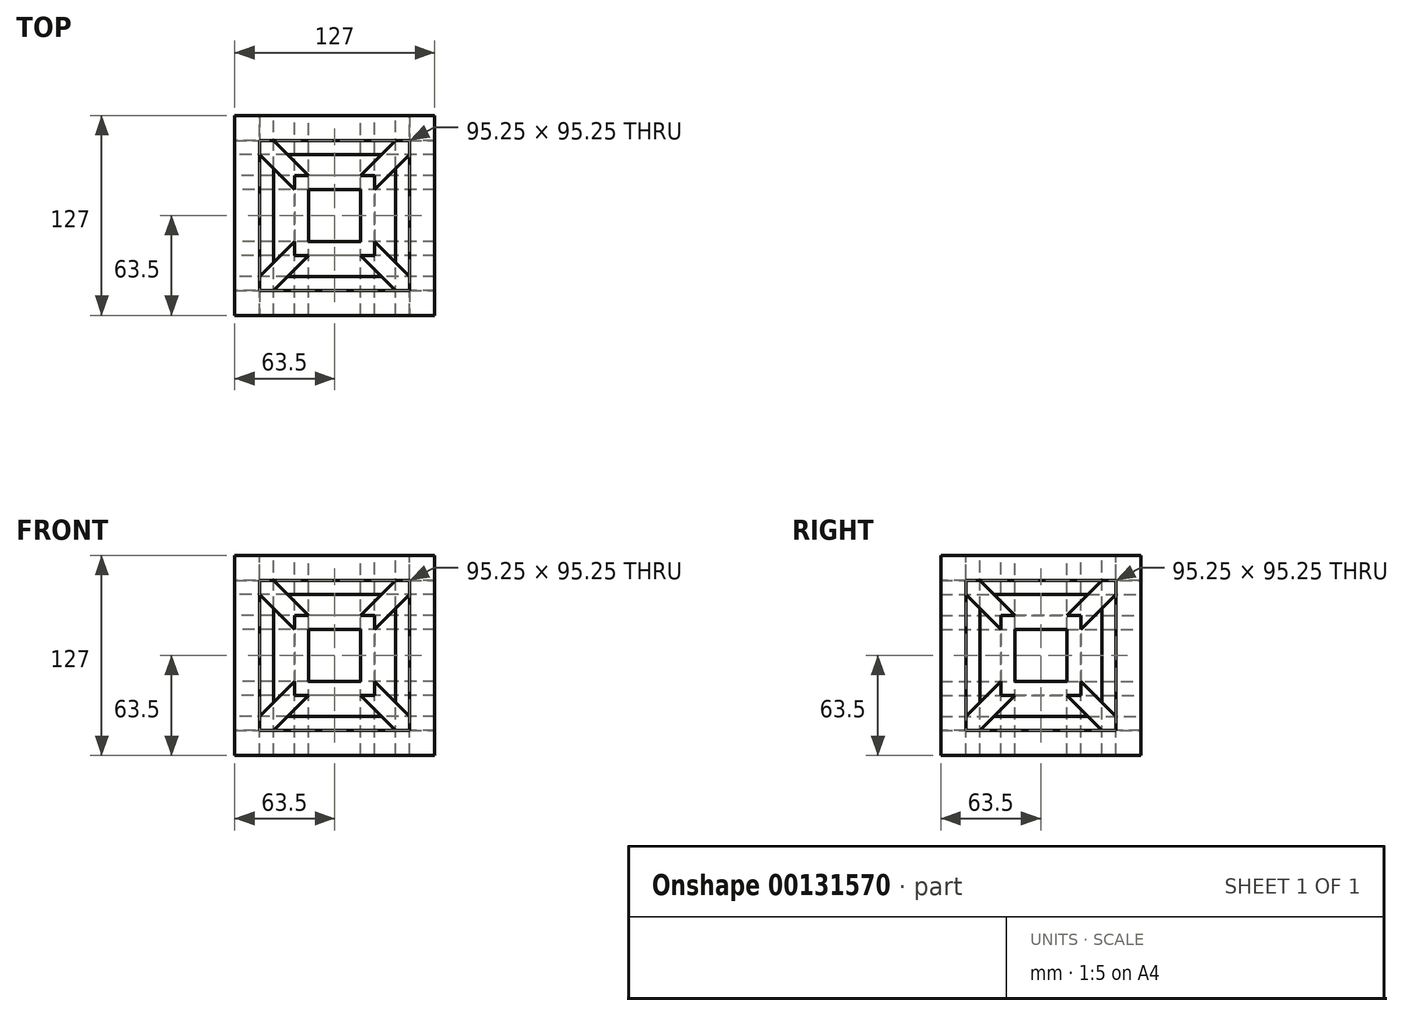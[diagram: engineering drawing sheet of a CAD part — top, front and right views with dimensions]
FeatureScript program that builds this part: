
annotation { "Feature Type Name" : "Feature", "Feature Type Description" : "" }
export const myFeature = defineFeature(function(context is Context, id is Id, definition is map)
    precondition{}
    {
        {
            var Q0;
            Q0=qCreatedBy(makeId("Front.planeOp"),FACE);
            var sketch = newSketch(context, id + "F0", { "sketchPlane" : qUnion([Q0])});
            skLineSegment(sketch, "E0.bottom", {"start": v(63.5, 63.5) * mm, "end": v(-63.5, 63.5) * mm});
            skLineSegment(sketch, "E0.top", {"start": v(63.5, -63.5) * mm, "end": v(-63.5, -63.5) * mm});
            skLineSegment(sketch, "E0.left", {"start": v(63.5, 63.5) * mm, "end": v(63.5, -63.5) * mm});
            skLineSegment(sketch, "E0.right", {"start": v(-63.5, 63.5) * mm, "end": v(-63.5, -63.5) * mm});
            skPoint(sketch, "E0.middle", {"position": v(0, 0) * mm});
            skSolve(sketch);
        }
        {
            var Q0;
            Q0 = qSketchRegion(id + "F0", true);
            extrude(context, id + "F1", {"entities" : qUnion([Q0]), "endBound" : BoundingType.SYMMETRIC, "depth" : 127 * mm});
        }
        {
            var Q0;
            Q0=makeQuery(id+"F1.opExtrude","CAP_FACE",FACE,{"disambiguationData":[OSD([sQuery(id+"F0.wireOp",EDGE,"E0.bottom"),sQuery(id+"F0.wireOp",EDGE,"E0.top"),sQuery(id+"F0.wireOp",EDGE,"E0.left"),sQuery(id+"F0.wireOp",EDGE,"E0.right")])],"isStart":false});
            var sketch = newSketch(context, id + "F2", { "sketchPlane" : qUnion([Q0])});
            skLineSegment(sketch, "E1.bottom", {"start": v(47.63, 47.63) * mm, "end": v(-47.63, 47.63) * mm});
            skLineSegment(sketch, "E1.top", {"start": v(47.63, -47.62) * mm, "end": v(-47.63, -47.62) * mm});
            skLineSegment(sketch, "E1.left", {"start": v(47.63, 47.63) * mm, "end": v(47.63, -47.62) * mm});
            skLineSegment(sketch, "E1.right", {"start": v(-47.63, 47.63) * mm, "end": v(-47.63, -47.62) * mm});
            skPoint(sketch, "E1.middle", {"position": v(0, 0) * mm});
            skSolve(sketch);
        }
        {
            var Q0;
            Q0=makeQuery(id+"F1.opExtrude","SWEPT_FACE",FACE,{"disambiguationData":[OSD([sQuery(id+"F0.wireOp",EDGE,"E0.left")])]});
            var sketch = newSketch(context, id + "F3", { "sketchPlane" : qUnion([Q0])});
            skLineSegment(sketch, "E2.bottom", {"start": v(47.63, 47.63) * mm, "end": v(-47.63, 47.62) * mm});
            skLineSegment(sketch, "E2.top", {"start": v(47.63, -47.62) * mm, "end": v(-47.63, -47.63) * mm});
            skLineSegment(sketch, "E2.left", {"start": v(47.63, 47.62) * mm, "end": v(47.63, -47.63) * mm});
            skLineSegment(sketch, "E2.right", {"start": v(-47.63, 47.62) * mm, "end": v(-47.63, -47.63) * mm});
            skPoint(sketch, "E2.middle", {"position": v(0, 0) * mm});
            skSolve(sketch);
        }
        {
            var Q0;
            Q0=makeQuery(id+"F3.imprint","IMPRINT",FACE,{"disambiguationData":[TD([[makeQuery(id+"F3.imprint","IMPRINT",EDGE,{"derivedFrom":sQuery(id+"F3.wireOp",EDGE,"E2.bottom")}),1.0]])]});
            extrude(context, id + "F4", {"entities" : qUnion([Q0]), "operationType" : NewBodyOperationType.REMOVE, "oppositeDirection" : true, "depth" : 127 * mm});
        }
        {
            var Q0;
            Q0 = qSketchRegion(id + "F2", true);
            extrude(context, id + "F5", {"entities" : qUnion([Q0]), "operationType" : NewBodyOperationType.REMOVE, "oppositeDirection" : true, "depth" : 127 * mm});
        }
        {
            var Q0;
            Q0=makeQuery(id+"F1.opExtrude","SWEPT_FACE",FACE,{"disambiguationData":[OSD([sQuery(id+"F0.wireOp",EDGE,"E0.bottom")])]});
            var sketch = newSketch(context, id + "F6", { "sketchPlane" : qUnion([Q0])});
            skLineSegment(sketch, "E3.bottom", {"start": v(47.63, 47.63) * mm, "end": v(-47.63, 47.63) * mm});
            skLineSegment(sketch, "E3.top", {"start": v(47.63, -47.62) * mm, "end": v(-47.63, -47.62) * mm});
            skLineSegment(sketch, "E3.left", {"start": v(47.63, 47.63) * mm, "end": v(47.63, -47.62) * mm});
            skLineSegment(sketch, "E3.right", {"start": v(-47.63, 47.63) * mm, "end": v(-47.63, -47.62) * mm});
            skPoint(sketch, "E3.middle", {"position": v(0, 0) * mm});
            skSolve(sketch);
        }
        {
            var Q0;
            Q0 = qSketchRegion(id + "F6", true);
            extrude(context, id + "F7", {"entities" : qUnion([Q0]), "operationType" : NewBodyOperationType.REMOVE, "oppositeDirection" : true, "depth" : 127 * mm});
        }
        {
            var Q0;
            Q0=qCreatedBy(makeId("Top.planeOp"),FACE);
            var sketch = newSketch(context, id + "F8", { "sketchPlane" : qUnion([Q0])});
            skLineSegment(sketch, "E4.bottom", {"start": v(25.4, 25.4) * mm, "end": v(-25.4, 25.4) * mm});
            skLineSegment(sketch, "E4.top", {"start": v(25.4, -25.4) * mm, "end": v(-25.4, -25.4) * mm});
            skLineSegment(sketch, "E4.left", {"start": v(25.4, 25.4) * mm, "end": v(25.4, -25.4) * mm});
            skLineSegment(sketch, "E4.right", {"start": v(-25.4, 25.4) * mm, "end": v(-25.4, -25.4) * mm});
            skPoint(sketch, "E4.middle", {"position": v(0, 0) * mm});
            skSolve(sketch);
        }
        {
            var Q0;
            Q0 = qSketchRegion(id + "F8", true);
            extrude(context, id + "F9", {"entities" : qUnion([Q0]), "endBound" : BoundingType.SYMMETRIC, "depth" : 50.8 * mm});
        }
        {
            var Q0;
            Q0=qCreatedBy(makeId("Right.planeOp"),FACE);
            var sketch = newSketch(context, id + "F10", { "sketchPlane" : qUnion([Q0])});
            skLineSegment(sketch, "E5.bottom", {"start": v(25.4, 25.4) * mm, "end": v(-25.4, 25.4) * mm});
            skLineSegment(sketch, "E5.top", {"start": v(25.4, -25.4) * mm, "end": v(-25.4, -25.4) * mm});
            skLineSegment(sketch, "E5.left", {"start": v(25.4, 25.4) * mm, "end": v(25.4, -25.4) * mm});
            skLineSegment(sketch, "E5.right", {"start": v(-25.4, 25.4) * mm, "end": v(-25.4, -25.4) * mm});
            skPoint(sketch, "E5.middle", {"position": v(0, 0) * mm});
            skLineSegment(sketch, "E6.bottom", {"start": v(47.62, 47.63) * mm, "end": v(-47.63, 47.62) * mm});
            skLineSegment(sketch, "E6.top", {"start": v(47.63, -47.62) * mm, "end": v(-47.63, -47.63) * mm});
            skLineSegment(sketch, "E6.left", {"start": v(47.63, 47.63) * mm, "end": v(47.63, -47.62) * mm});
            skLineSegment(sketch, "E6.right", {"start": v(-47.63, 47.62) * mm, "end": v(-47.63, -47.63) * mm});
            skLineSegment(sketch, "E7", {"start": v(-16.5, 25.4) * mm, "end": v(-38.74, 47.62) * mm});
            skLineSegment(sketch, "E8", {"start": v(-25.4, 16.51) * mm, "end": v(-47.63, 38.73) * mm});
            skLineSegment(sketch, "E9", {"start": v(16.5, 25.4) * mm, "end": v(38.74, 47.63) * mm});
            skLineSegment(sketch, "E10", {"start": v(25.4, 16.51) * mm, "end": v(47.63, 38.73) * mm});
            skLineSegment(sketch, "E11", {"start": v(-25.4, -16.5) * mm, "end": v(-47.63, -38.74) * mm});
            skLineSegment(sketch, "E12", {"start": v(-16.5, -25.4) * mm, "end": v(-38.74, -47.63) * mm});
            skLineSegment(sketch, "E13", {"start": v(16.5, -25.4) * mm, "end": v(38.74, -47.62) * mm});
            skLineSegment(sketch, "E14", {"start": v(25.4, -16.5) * mm, "end": v(47.63, -38.74) * mm});
            skSolve(sketch);
        }
        {
            var Q0;
            {var subQ7=sQuery(id+"F10.wireOp",EDGE,"E7");Q0=makeQuery(id+"F10.imprint","IMPRINT",FACE,{"disambiguationData":[TD([[makeQuery(id+"F10.imprint","IMPRINT",EDGE,{"derivedFrom":subQ7}),1.0]])]});}
            var Q1;
            {var subQ4=sQuery(id+"F10.wireOp",EDGE,"E9");Q1=makeQuery(id+"F10.imprint","IMPRINT",FACE,{"disambiguationData":[TD([[makeQuery(id+"F10.imprint","IMPRINT",EDGE,{"derivedFrom":subQ4}),-1.0]])]});}
            var Q2;
            {var subQ7=sQuery(id+"F10.wireOp",EDGE,"E13");Q2=makeQuery(id+"F10.imprint","IMPRINT",FACE,{"disambiguationData":[TD([[makeQuery(id+"F10.imprint","IMPRINT",EDGE,{"derivedFrom":subQ7}),1.0]])]});}
            var Q3;
            {var subQ3=sQuery(id+"F10.wireOp",EDGE,"E11");Q3=makeQuery(id+"F10.imprint","IMPRINT",FACE,{"disambiguationData":[TD([[makeQuery(id+"F10.imprint","IMPRINT",EDGE,{"derivedFrom":subQ3}),1.0]])]});}
            extrude(context, id + "F11", {"entities" : qUnion([Q0, Q1, Q2, Q3]), "endBound" : BoundingType.SYMMETRIC, "depth" : 127 * mm});
        }
        {
            var Q0;
            Q0=qCreatedBy(makeId("Top.planeOp"),FACE);
            var sketch = newSketch(context, id + "F12", { "sketchPlane" : qUnion([Q0])});
            skLineSegment(sketch, "E15.bottom", {"start": v(25.4, 25.4) * mm, "end": v(-25.4, 25.4) * mm});
            skLineSegment(sketch, "E15.top", {"start": v(25.4, -25.4) * mm, "end": v(-25.4, -25.4) * mm});
            skLineSegment(sketch, "E15.left", {"start": v(25.4, 25.4) * mm, "end": v(25.4, -25.4) * mm});
            skLineSegment(sketch, "E15.right", {"start": v(-25.4, 25.4) * mm, "end": v(-25.4, -25.4) * mm});
            skPoint(sketch, "E15.middle", {"position": v(0, 0) * mm});
            skLineSegment(sketch, "E16.bottom", {"start": v(47.63, 47.63) * mm, "end": v(-47.63, 47.62) * mm});
            skLineSegment(sketch, "E16.top", {"start": v(47.63, -47.62) * mm, "end": v(-47.63, -47.63) * mm});
            skLineSegment(sketch, "E16.left", {"start": v(47.63, 47.63) * mm, "end": v(47.63, -47.62) * mm});
            skLineSegment(sketch, "E16.right", {"start": v(-47.63, 47.62) * mm, "end": v(-47.63, -47.63) * mm});
            skLineSegment(sketch, "E17", {"start": v(-16.5, 25.4) * mm, "end": v(-38.74, 47.63) * mm});
            skLineSegment(sketch, "E18", {"start": v(-25.4, 16.5) * mm, "end": v(-47.63, 38.74) * mm});
            skLineSegment(sketch, "E19", {"start": v(16.5, 25.4) * mm, "end": v(38.74, 47.63) * mm});
            skLineSegment(sketch, "E20", {"start": v(25.4, 16.5) * mm, "end": v(47.62, 38.74) * mm});
            skLineSegment(sketch, "E21", {"start": v(-25.4, -16.5) * mm, "end": v(-47.63, -38.74) * mm});
            skLineSegment(sketch, "E22", {"start": v(-16.51, -25.4) * mm, "end": v(-38.74, -47.63) * mm});
            skLineSegment(sketch, "E23", {"start": v(16.5, -25.4) * mm, "end": v(38.74, -47.63) * mm});
            skLineSegment(sketch, "E24", {"start": v(25.4, -16.5) * mm, "end": v(47.62, -38.73) * mm});
            skSolve(sketch);
        }
        {
            var Q0;
            {var subQ4=sQuery(id+"F12.wireOp",EDGE,"E19");Q0=makeQuery(id+"F12.imprint","IMPRINT",FACE,{"disambiguationData":[TD([[makeQuery(id+"F12.imprint","IMPRINT",EDGE,{"derivedFrom":subQ4}),-1.0]])]});}
            var Q1;
            {var subQ4=sQuery(id+"F12.wireOp",EDGE,"E23");Q1=makeQuery(id+"F12.imprint","IMPRINT",FACE,{"disambiguationData":[TD([[makeQuery(id+"F12.imprint","IMPRINT",EDGE,{"derivedFrom":subQ4}),1.0]])]});}
            var Q2;
            {var subQ3=sQuery(id+"F12.wireOp",EDGE,"E21");Q2=makeQuery(id+"F12.imprint","IMPRINT",FACE,{"disambiguationData":[TD([[makeQuery(id+"F12.imprint","IMPRINT",EDGE,{"derivedFrom":subQ3}),1.0]])]});}
            var Q3;
            {var subQ4=sQuery(id+"F12.wireOp",EDGE,"E17");Q3=makeQuery(id+"F12.imprint","IMPRINT",FACE,{"disambiguationData":[TD([[makeQuery(id+"F12.imprint","IMPRINT",EDGE,{"derivedFrom":subQ4}),1.0]])]});}
            extrude(context, id + "F13", {"entities" : qUnion([Q0, Q1, Q2, Q3]), "endBound" : BoundingType.SYMMETRIC, "oppositeDirection" : true, "depth" : 127 * mm});
        }
        {
            var Q0;
            Q0=qCreatedBy(makeId("Front.planeOp"),FACE);
            var sketch = newSketch(context, id + "F14", { "sketchPlane" : qUnion([Q0])});
            skLineSegment(sketch, "E25.bottom", {"start": v(-25.4, 25.4) * mm, "end": v(25.4, 25.4) * mm});
            skLineSegment(sketch, "E25.top", {"start": v(-25.4, -25.4) * mm, "end": v(25.4, -25.4) * mm});
            skLineSegment(sketch, "E25.left", {"start": v(-25.4, 25.4) * mm, "end": v(-25.4, -25.4) * mm});
            skLineSegment(sketch, "E25.right", {"start": v(25.4, 25.4) * mm, "end": v(25.4, -25.4) * mm});
            skPoint(sketch, "E25.middle", {"position": v(0, 0) * mm});
            skLineSegment(sketch, "E26.bottom", {"start": v(-47.63, 47.63) * mm, "end": v(47.63, 47.63) * mm});
            skLineSegment(sketch, "E26.top", {"start": v(-47.63, -47.63) * mm, "end": v(47.62, -47.63) * mm});
            skLineSegment(sketch, "E26.left", {"start": v(-47.63, 47.63) * mm, "end": v(-47.63, -47.63) * mm});
            skLineSegment(sketch, "E26.right", {"start": v(47.63, 47.63) * mm, "end": v(47.62, -47.63) * mm});
            skLineSegment(sketch, "E27", {"start": v(38.74, 47.62) * mm, "end": v(16.51, 25.4) * mm});
            skLineSegment(sketch, "E28", {"start": v(25.4, 16.5) * mm, "end": v(47.63, 38.74) * mm});
            skLineSegment(sketch, "E29", {"start": v(-16.51, 25.4) * mm, "end": v(-38.74, 47.62) * mm});
            skLineSegment(sketch, "E30", {"start": v(-25.4, 16.5) * mm, "end": v(-47.63, 38.73) * mm});
            skLineSegment(sketch, "E31", {"start": v(25.4, -16.5) * mm, "end": v(47.62, -38.74) * mm});
            skLineSegment(sketch, "E32", {"start": v(16.51, -25.4) * mm, "end": v(38.73, -47.63) * mm});
            skLineSegment(sketch, "E33", {"start": v(-16.51, -25.4) * mm, "end": v(-38.74, -47.62) * mm});
            skLineSegment(sketch, "E34", {"start": v(-25.4, -16.51) * mm, "end": v(-47.63, -38.74) * mm});
            skSolve(sketch);
        }
        {
            var Q0;
            {var subQ7=sQuery(id+"F14.wireOp",EDGE,"E29");Q0=makeQuery(id+"F14.imprint","IMPRINT",FACE,{"disambiguationData":[TD([[makeQuery(id+"F14.imprint","IMPRINT",EDGE,{"derivedFrom":subQ7}),1.0]])]});}
            var Q1;
            {var subQ7=sQuery(id+"F14.wireOp",EDGE,"E27");Q1=makeQuery(id+"F14.imprint","IMPRINT",FACE,{"disambiguationData":[TD([[makeQuery(id+"F14.imprint","IMPRINT",EDGE,{"derivedFrom":subQ7}),1.0]])]});}
            var Q2;
            {var subQ4=sQuery(id+"F14.wireOp",EDGE,"E33");Q2=makeQuery(id+"F14.imprint","IMPRINT",FACE,{"disambiguationData":[TD([[makeQuery(id+"F14.imprint","IMPRINT",EDGE,{"derivedFrom":subQ4}),-1.0]])]});}
            var Q3;
            {var subQ3=sQuery(id+"F14.wireOp",EDGE,"E31");Q3=makeQuery(id+"F14.imprint","IMPRINT",FACE,{"disambiguationData":[TD([[makeQuery(id+"F14.imprint","IMPRINT",EDGE,{"derivedFrom":subQ3}),-1.0]])]});}
            extrude(context, id + "F15", {"entities" : qUnion([Q0, Q1, Q2, Q3]), "endBound" : BoundingType.SYMMETRIC, "depth" : 127 * mm});
        }
    });
